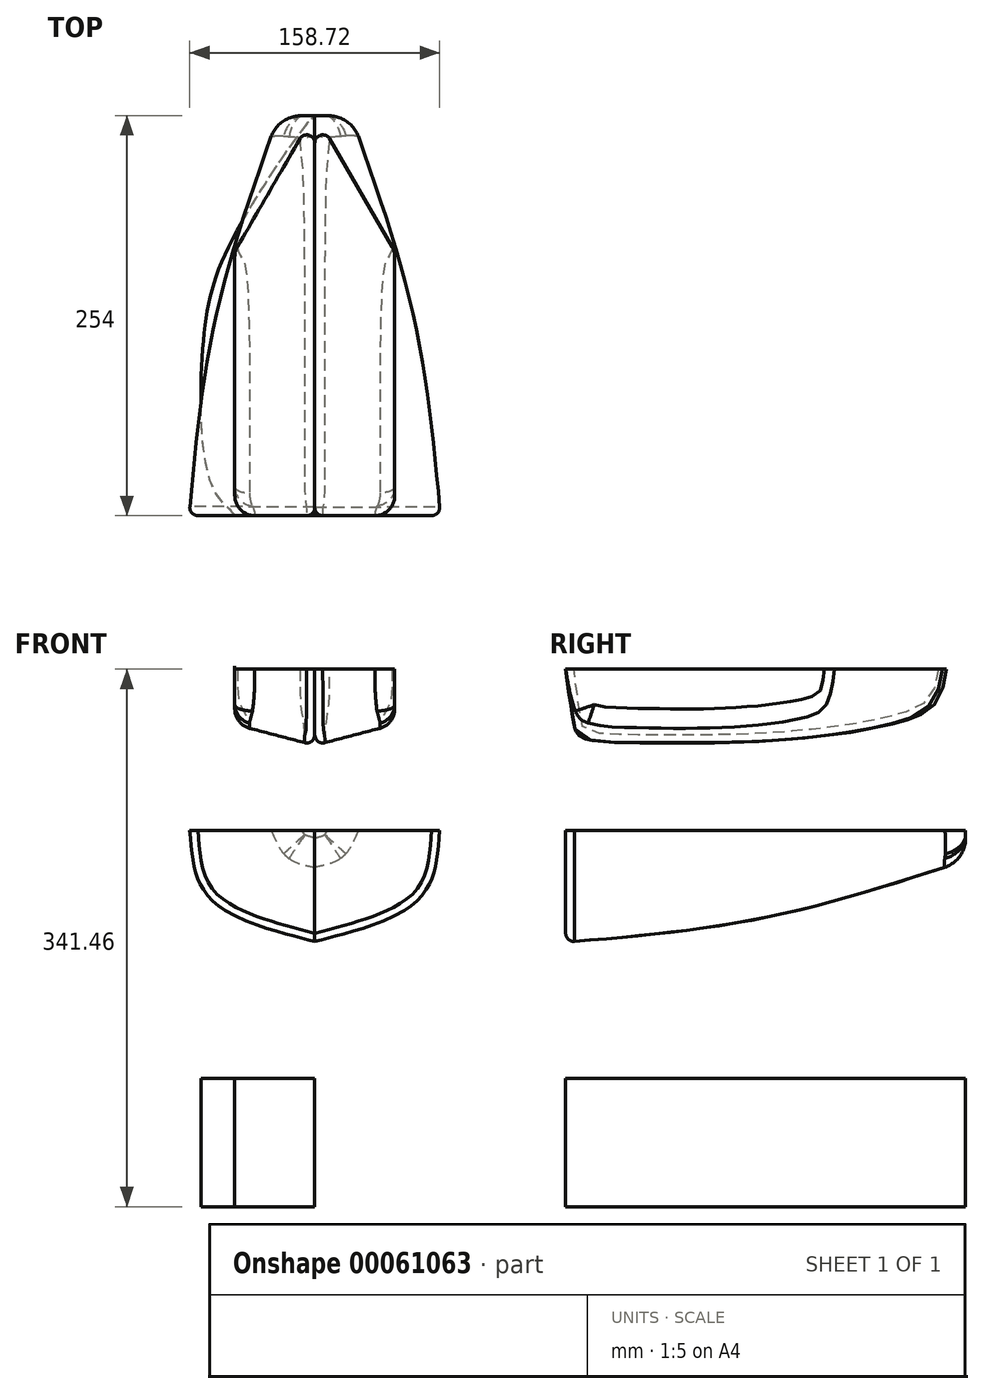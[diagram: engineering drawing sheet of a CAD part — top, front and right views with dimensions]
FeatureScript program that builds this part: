
annotation { "Feature Type Name" : "Feature", "Feature Type Description" : "" }
export const myFeature = defineFeature(function(context is Context, id is Id, definition is map)
    precondition{}
    {
        {
            var Q0;
            Q0=qCreatedBy(makeId("Top.planeOp"),FACE);
            var sketch = newSketch(context, id + "F0", { "sketchPlane" : qUnion([Q0])});
            skLineSegment(sketch, "E0", {"start": v(0, 63.8) * mm, "end": v(0, -70.22) * mm, "construction": true});
            skLineSegment(sketch, "E1", {"start": v(0, 0) * mm, "end": v(-50.8, 0) * mm});
            skFitSpline(sketch, "E2", {"points": [v(-50.8, 0) * mm, v(-63.5, 15.33) * mm, v(-71.1, 106.58) * mm, v(-50.67, 178.4) * mm, v(0, 254) * mm], "startDerivative": vector(-23.2, 62.66) * mm, "endDerivative": vector(52.1, 32.05) * mm});
            skLineSegment(sketch, "E3", {"start": v(0, 0) * mm, "end": v(0, 254) * mm});
            skSolve(sketch);
        }
        {
            var Q0;
            Q0=qCreatedBy(makeId("Right.planeOp"),FACE);
            var sketch = newSketch(context, id + "F1", { "sketchPlane" : qUnion([Q0])});
            skLineSegment(sketch, "E4", {"start": v(0, 0) * mm, "end": v(0, -64.3) * mm});
            skFitSpline(sketch, "E5", {"points": [v(0, -64.3) * mm, v(68.95, -64.3) * mm, v(117.46, -60.38) * mm, v(176.93, -53.73) * mm, v(238.74, -37.7) * mm, v(254, 0) * mm], "startDerivative": vector(324.49, -3.56) * mm, "endDerivative": vector(62.34, 229.36) * mm});
            skLineSegment(sketch, "E6", {"start": v(0, 0) * mm, "end": v(254, 0) * mm});
            skSolve(sketch);
        }
        {
            var Q0;
            Q0=makeQuery(id+"FCQlBqhY4ovq98z_0.opLoft","SWEPT_FACE",FACE,{"disambiguationData":[OSD([sQuery(id+"F0.wireOp",VERTEX,"E2.start"),sQuery(id+"F0.wireOp",VERTEX,"E2.end"),sQuery(id+"F0.wireOp",VERTEX,"203ff89f-79ef-4870-bf09-8534a42910c50.MirrorCS.start"),sQuery(id+"F0.wireOp",VERTEX,"203ff89f-79ef-4870-bf09-8534a42910c50.MirrorCS.end"),sQuery(id+"F0.wireOp",EDGE,"E2"),sQuery(id+"F0.wireOp",EDGE,"203ff89f-79ef-4870-bf09-8534a42910c50.MirrorCS")])]});
            var Q1;
            Q1=makeQuery(id+"F0.imprint","IMPRINT",FACE,{"disambiguationData":[TD([[makeQuery(id+"F0.imprint","IMPRINT",EDGE,{"derivedFrom":sQuery(id+"F0.wireOp",EDGE,"E1")}),-1.0]])]});
            extrude(context, id + "F2", {"entities" : qUnion([Q0, Q1]), "oppositeDirection" : true, "depth" : 81.47 * mm});
        }
        {
            var Q0;
            Q0=sQuery(id+"F0.wireOp",EDGE,"E2");
            var Q1;
            Q1=sQuery(id+"F1.wireOp",EDGE,"E5");
            loft(context, id + "F3", {"bodyType" : ToolBodyType.SURFACE, "operationType" : NewBodyOperationType.REMOVE, "wireProfilesArray" : [{ "wireProfileEntities" : qUnion([Q0]) }, { "wireProfileEntities" : qUnion([Q1]) }]});
        }
        {
            var Q0;
            Q0=qCreatedBy(makeId("Front.planeOp"),FACE);
            cPlane(context, id + "F4", {"entities" : qUnion([Q0]), "cplaneType" : CPlaneType.OFFSET, "offset" : 127 * mm, "oppositeDirection" : true, "width" : 152.4 * mm, "height" : 152.4 * mm});
        }
        {
            var Q0;
            Q0=qCreatedBy(id+"F4.planeOp",FACE);
            cPlane(context, id + "F5", {"entities" : qUnion([Q0]), "cplaneType" : CPlaneType.OFFSET, "offset" : 127 * mm, "oppositeDirection" : true, "width" : 152.4 * mm, "height" : 152.4 * mm});
        }
        {
            var Q0;
            Q0=qCreatedBy(makeId("Front.planeOp"),FACE);
            var sketch = newSketch(context, id + "F6", { "sketchPlane" : qUnion([Q0])});
            skLineSegment(sketch, "E7", {"start": v(0, 0) * mm, "end": v(0, 157.5) * mm, "construction": true});
            skLineSegment(sketch, "E8", {"start": v(0, 157.5) * mm, "end": v(-79.85, 157.5) * mm});
            skLineSegment(sketch, "E9", {"start": v(0, 157.5) * mm, "end": v(0, 86.5) * mm});
            skFitSpline(sketch, "E10", {"points": [v(-79.85, 157.5) * mm, v(-68.02, 115.1) * mm, v(0, 86.5) * mm], "startDerivative": vector(6.8, -107.44) * mm, "endDerivative": vector(146.91, -37.52) * mm});
            skSolve(sketch);
        }
        {
            var Q0;
            Q0=qCreatedBy(id+"F4.planeOp",FACE);
            var sketch = newSketch(context, id + "F7", { "sketchPlane" : qUnion([Q0])});
            skLineSegment(sketch, "E11.0", {"start": v(0, 157.5) * mm, "end": v(0, 102.28) * mm});
            skLineSegment(sketch, "E12.0", {"start": v(0, 157.5) * mm, "end": v(-62.6, 157.5) * mm});
            skFitSpline(sketch, "E13", {"points": [v(-62.6, 157.5) * mm, v(-49.79, 124.46) * mm, v(0, 102.28) * mm], "startDerivative": vector(15.05, -81.56) * mm, "endDerivative": vector(106.87, -30.67) * mm});
            skPoint(sketch, "E14.orphan", {"position": v(0, 86.5) * mm});
            skPoint(sketch, "E15.orphan", {"position": v(-79.85, 157.5) * mm});
            skSolve(sketch);
        }
        {
            var Q0;
            Q0=qCreatedBy(id+"F5.planeOp",FACE);
            var sketch = newSketch(context, id + "F8", { "sketchPlane" : qUnion([Q0])});
            skLineSegment(sketch, "E16.0", {"start": v(0, 157.5) * mm, "end": v(0, 138.38) * mm});
            skFitSpline(sketch, "E17", {"points": [v(-23, 157.5) * mm, v(-13.94, 143.26) * mm, v(0, 138.38) * mm], "startDerivative": vector(14.62, -32.06) * mm, "endDerivative": vector(31.58, -5.88) * mm});
            skPoint(sketch, "E18.orphan", {"position": v(0, 86.5) * mm});
            skPoint(sketch, "E19.orphan", {"position": v(-79.85, 157.5) * mm});
            skPoint(sketch, "E20.0.start.orphan", {"position": v(0, 157.5) * mm});
            skLineSegment(sketch, "E21", {"start": v(0, 157.5) * mm, "end": v(-23, 157.5) * mm});
            skSolve(sketch);
        }
        {
            var Q0;
            Q0=makeQuery(id+"F6.imprint","IMPRINT",FACE,{"disambiguationData":[TD([[makeQuery(id+"F6.imprint","IMPRINT",EDGE,{"derivedFrom":sQuery(id+"F6.wireOp",EDGE,"E8")}),1.0]])]});
            var Q1;
            Q1=makeQuery(id+"F7.imprint","IMPRINT",FACE,{"disambiguationData":[TD([[makeQuery(id+"F7.imprint","IMPRINT",EDGE,{"derivedFrom":sQuery(id+"F7.wireOp",EDGE,"E11.0")}),-1.0]])]});
            var Q2;
            Q2=makeQuery(id+"F8.imprint","IMPRINT",FACE,{"disambiguationData":[TD([[makeQuery(id+"F8.imprint","IMPRINT",EDGE,{"derivedFrom":sQuery(id+"F8.wireOp",EDGE,"E16.0")}),-1.0]])]});
            loft(context, id + "F9", {"sheetProfilesArray" : [{ "sheetProfileEntities" : qUnion([Q0]) }, { "sheetProfileEntities" : qUnion([Q1]) }, { "sheetProfileEntities" : qUnion([Q2]) }]});
        }
        {
            var Q0;
            {var subQ0=sQuery(id+"F6.wireOp",EDGE,"E10");var subQ1=sQuery(id+"F6.wireOp",EDGE,"E9");var subQ2=sQuery(id+"F6.wireOp",EDGE,"E8");Q0=makeQuery(id+"F9.opLoft","MID_CAP_EDGE",EDGE,{"disambiguationData":[OSD([subQ2,subQ1,subQ0]),TDD([makeQuery(id+"F6.imprint","INTERSECT",VERTEX,{"derivedFrom":[subQ2,subQ0]}),makeQuery(id+"F6.imprint","INTERSECT",VERTEX,{"derivedFrom":[subQ1,subQ0]}),makeQuery(id+"F6.imprint","IMPRINT",EDGE,{"derivedFrom":subQ0})])],"capPos":0.0});}
            fillet(context, id + "F10", {"entities" : qUnion([Q0]), "radius" : 5.08 * mm, "tangentPropagation" : true, "allowEdgeOverflow" : false});
        }
        {
            var Q0;
            {var subQ0=sQuery(id+"F8.wireOp",EDGE,"E17");var subQ1=sQuery(id+"F8.wireOp",EDGE,"E21");var subQ2=sQuery(id+"F8.wireOp",EDGE,"E16.0");Q0=makeQuery(id+"F9.opLoft","MID_CAP_EDGE",EDGE,{"disambiguationData":[OSD([subQ2,subQ0,subQ1]),TDD([makeQuery(id+"F8.imprint","INTERSECT",VERTEX,{"derivedFrom":[subQ2,subQ0]}),makeQuery(id+"F8.imprint","INTERSECT",VERTEX,{"derivedFrom":[subQ0,subQ1]}),makeQuery(id+"F8.imprint","IMPRINT",EDGE,{"derivedFrom":subQ0})])],"capPos":2.0});}
            fillet(context, id + "F11", {"entities" : qUnion([Q0]), "radius" : 19.05 * mm, "tangentPropagation" : true, "allowEdgeOverflow" : false});
        }
        {
            var Q0;
            Q0=makeQuery(id+"F9.opLoft","SWEPT_BODY",BODY,{"disambiguationData":[OSD([makeQuery(id+"F6.imprint","IMPRINT",FACE,{"disambiguationData":[TD([[makeQuery(id+"F6.imprint","IMPRINT",EDGE,{"derivedFrom":sQuery(id+"F6.wireOp",EDGE,"E8")}),1.0]])]}),sQuery(id+"F7.wireOp",EDGE,"E12.0"),makeQuery(id+"F8.imprint","IMPRINT",FACE,{"disambiguationData":[TD([[makeQuery(id+"F8.imprint","IMPRINT",EDGE,{"derivedFrom":sQuery(id+"F8.wireOp",EDGE,"E16.0")}),-1.0]])]})])]});
            var Q1;
            Q1=qCreatedBy(makeId("Right.planeOp"),FACE);
            mirror(context, id + "F12", {"operationType" : NewBodyOperationType.ADD, "entities" : qUnion([Q0]), "mirrorPlane" : qUnion([Q1])});
        }
        {
            var Q0;
            Q0=qCreatedBy(makeId("Right.planeOp"),FACE);
            var sketch = newSketch(context, id + "F13", { "sketchPlane" : qUnion([Q0])});
            skLineSegment(sketch, "E22", {"start": v(0, 259.99) * mm, "end": v(255.65, 259.99) * mm});
            skFitSpline(sketch, "E23", {"points": [v(255.65, 259.99) * mm, v(249.6, 240.33) * mm, v(222.37, 225.7) * mm, v(135.66, 213.1) * mm, v(50.46, 211.6) * mm, v(9.63, 215.12) * mm, v(5.1, 223.7) * mm, v(0, 259.99) * mm], "startDerivative": vector(-30.67, -207.72) * mm, "endDerivative": vector(-39.54, 308.61) * mm});
            skSolve(sketch);
        }
        {
            var Q0;
            Q0=qCreatedBy(makeId("Right.planeOp"),FACE);
            cPlane(context, id + "F14", {"entities" : qUnion([Q0]), "cplaneType" : CPlaneType.OFFSET, "offset" : 50.8 * mm, "width" : 152.4 * mm, "height" : 152.4 * mm});
        }
        {
            var Q0;
            Q0=qCreatedBy(id+"F14.planeOp",FACE);
            var sketch = newSketch(context, id + "F15", { "sketchPlane" : qUnion([Q0])});
            skLineSegment(sketch, "E24", {"start": v(0, 259.99) * mm, "end": v(167.83, 259.99) * mm});
            skFitSpline(sketch, "E25", {"points": [v(167.83, 259.99) * mm, v(163.3, 241.4) * mm, v(147.14, 231.82) * mm, v(96.23, 225.28) * mm, v(44.6, 225.32) * mm, v(11.54, 229.8) * mm, v(5.53, 238.5) * mm, v(0, 259.99) * mm], "startDerivative": vector(-18.87, -176.44) * mm, "endDerivative": vector(-47.73, 310.1) * mm});
            skSolve(sketch);
        }
        {
            var Q0;
            Q0=makeQuery(id+"F13.imprint","IMPRINT",FACE,{"disambiguationData":[TD([[makeQuery(id+"F13.imprint","IMPRINT",EDGE,{"derivedFrom":sQuery(id+"F13.wireOp",EDGE,"E22")}),-1.0]])]});
            var Q1;
            Q1=makeQuery(id+"F15.imprint","IMPRINT",FACE,{"disambiguationData":[TD([[makeQuery(id+"F15.imprint","IMPRINT",EDGE,{"derivedFrom":sQuery(id+"F15.wireOp",EDGE,"E24")}),-1.0]])]});
            loft(context, id + "F16", {"sheetProfilesArray" : [{ "sheetProfileEntities" : qUnion([Q0]) }, { "sheetProfileEntities" : qUnion([Q1]) }]});
        }
        {
            var Q0;
            {var subQ0=sQuery(id+"F15.wireOp",EDGE,"E25");var subQ1=sQuery(id+"F15.wireOp",EDGE,"E24");Q0=makeQuery(id+"F16.opLoft","MID_CAP_EDGE",EDGE,{"disambiguationData":[OSD([subQ1,subQ0]),TDD([makeQuery(id+"F15.imprint","INTERSECT",VERTEX,{"disambiguationData":[OD(0.0)],"derivedFrom":[subQ1,subQ0]}),makeQuery(id+"F15.imprint","INTERSECT",VERTEX,{"disambiguationData":[OD(1.0)],"derivedFrom":[subQ1,subQ0]}),makeQuery(id+"F15.imprint","IMPRINT",EDGE,{"derivedFrom":subQ0})])],"capPos":1.0});}
            fillet(context, id + "F17", {"entities" : qUnion([Q0]), "radius" : 12.7 * mm, "tangentPropagation" : true, "allowEdgeOverflow" : false});
        }
        {
            var Q0;
            Q0=makeQuery(id+"F16.opLoft","SWEPT_BODY",BODY,{"disambiguationData":[OSD([makeQuery(id+"F13.imprint","IMPRINT",FACE,{"disambiguationData":[TD([[makeQuery(id+"F13.imprint","IMPRINT",EDGE,{"derivedFrom":sQuery(id+"F13.wireOp",EDGE,"E22")}),-1.0]])]}),makeQuery(id+"F15.imprint","IMPRINT",FACE,{"disambiguationData":[TD([[makeQuery(id+"F15.imprint","IMPRINT",EDGE,{"derivedFrom":sQuery(id+"F15.wireOp",EDGE,"E24")}),-1.0]])]})])]});
            var Q1;
            Q1=qCreatedBy(makeId("Right.planeOp"),FACE);
            mirror(context, id + "F18", {"operationType" : NewBodyOperationType.ADD, "entities" : qUnion([Q0]), "mirrorPlane" : qUnion([Q1])});
        }
        {
            var Q0;
            {var subQ0=sQuery(id+"F13.wireOp",EDGE,"E23");var subQ1=sQuery(id+"F13.wireOp",EDGE,"E22");var subQ2=makeQuery(id+"F16.opLoft","MID_CAP_EDGE",EDGE,{"disambiguationData":[OSD([subQ1,subQ0]),TDD([makeQuery(id+"F13.imprint","INTERSECT",VERTEX,{"disambiguationData":[OD(0.0)],"derivedFrom":[subQ1,subQ0]}),makeQuery(id+"F13.imprint","INTERSECT",VERTEX,{"disambiguationData":[OD(1.0)],"derivedFrom":[subQ1,subQ0]}),makeQuery(id+"F13.imprint","IMPRINT",EDGE,{"derivedFrom":subQ0})])],"capPos":0.0});Q0=makeQuery(id+"F18.boolean.opBoolean","MERGE",EDGE,{"derivedFrom":[subQ2,makeQuery(id+"F18.opPattern","COPY",EDGE,{"derivedFrom":subQ2,"instanceName":"1"})]});}
            fillet(context, id + "F19", {"entities" : qUnion([Q0]), "radius" : 5.08 * mm, "tangentPropagation" : true, "allowEdgeOverflow" : false});
        }
    });
